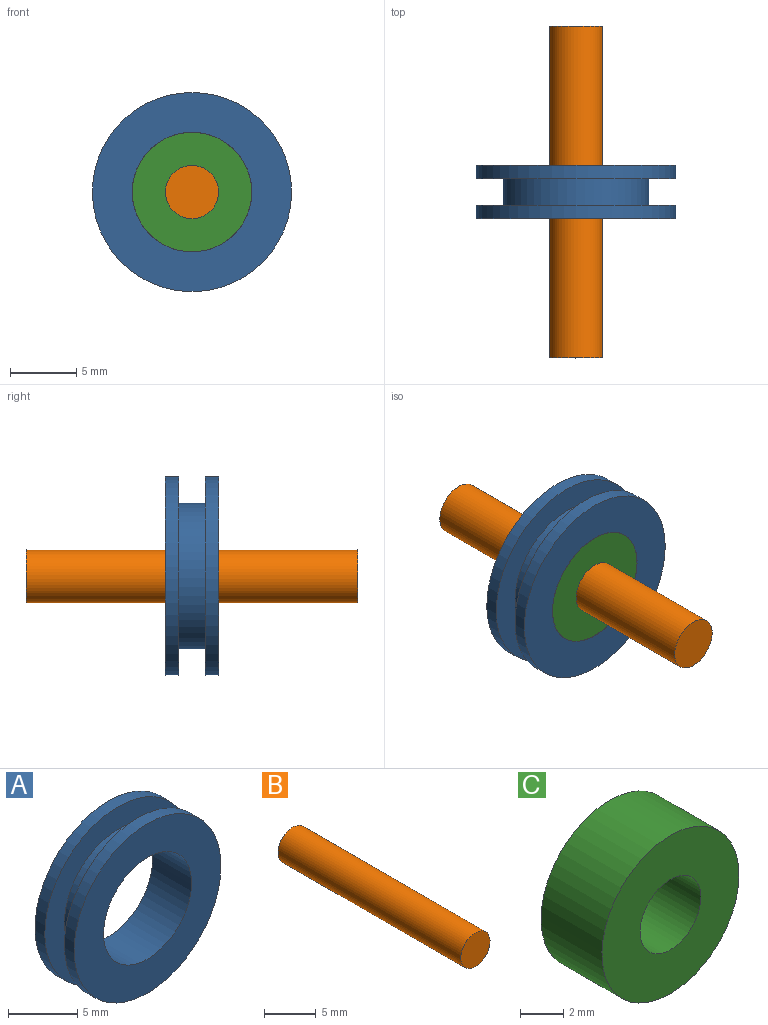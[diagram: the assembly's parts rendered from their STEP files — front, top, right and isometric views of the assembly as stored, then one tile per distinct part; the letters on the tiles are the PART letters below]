
ASSEMBLY  parts=3 mates=2
PART A: 8 faces, bbox 15x4x15 mm
  f0: plane 15x15mm, normal (0,-1,0), area 113.1mm2, adj f1,f7
  f1: cylinder r=4.5mm len=9mm, axis (0,1,0), area 113.1mm2, adj f0,f2
  f2: plane 15x15mm, normal (0,1,0), area 113.1mm2, adj f1,f3
  f3: cylinder r=7.5mm len=15mm, axis (0,1,0), area 47.1mm2, adj f2,f4
  f4: plane 15x15mm, normal (0,-1,0), area 81.7mm2, adj f3,f5
  f5: cylinder r=5.5mm len=11mm, axis (0,1,0), area 69.1mm2, adj f4,f6
  f6: plane 15x15mm, normal (0,1,0), area 81.7mm2, adj f5,f7
  f7: cylinder r=7.5mm len=15mm, axis (0,1,0), area 47.1mm2, adj f0,f6
PART B: 3 faces, bbox 4x25x4 mm
  f0: cylinder r=2mm len=25mm, axis (0,1,0), area 314.2mm2, adj f1,f2
  f1: plane 4x4mm, normal (0,-1,0), area 12.6mm2, adj f0
  f2: plane 4x4mm, normal (0,1,0), area 12.6mm2, adj f0
PART C: 4 faces, bbox 9x4x9 mm
  f0: cylinder r=2mm len=4mm, axis (0,1,0), area 50.3mm2, adj f2,f3
  f1: cylinder r=4.5mm len=9mm, axis (0,1,0), area 113.1mm2, adj f2,f3
  f2: plane 9x9mm, normal (0,-1,0), area 51.1mm2, adj f0,f1
  f3: plane 9x9mm, normal (0,1,0), area 51.1mm2, adj f0,f1
PLACE A t=(14.55,3.69,-4.88)mm
PLACE B t=(14.55,5.69,-4.88)mm
PLACE C t=(14.55,3.69,-4.88)mm
MATE revolute A.f1 <-> B.f0  axis (0,-1,0) through (-38.69,1.79,15.96)mm
MATE revolute C.f0 <-> A.f1  axis (0,-1,0) through (-38.69,1.79,15.96)mm
